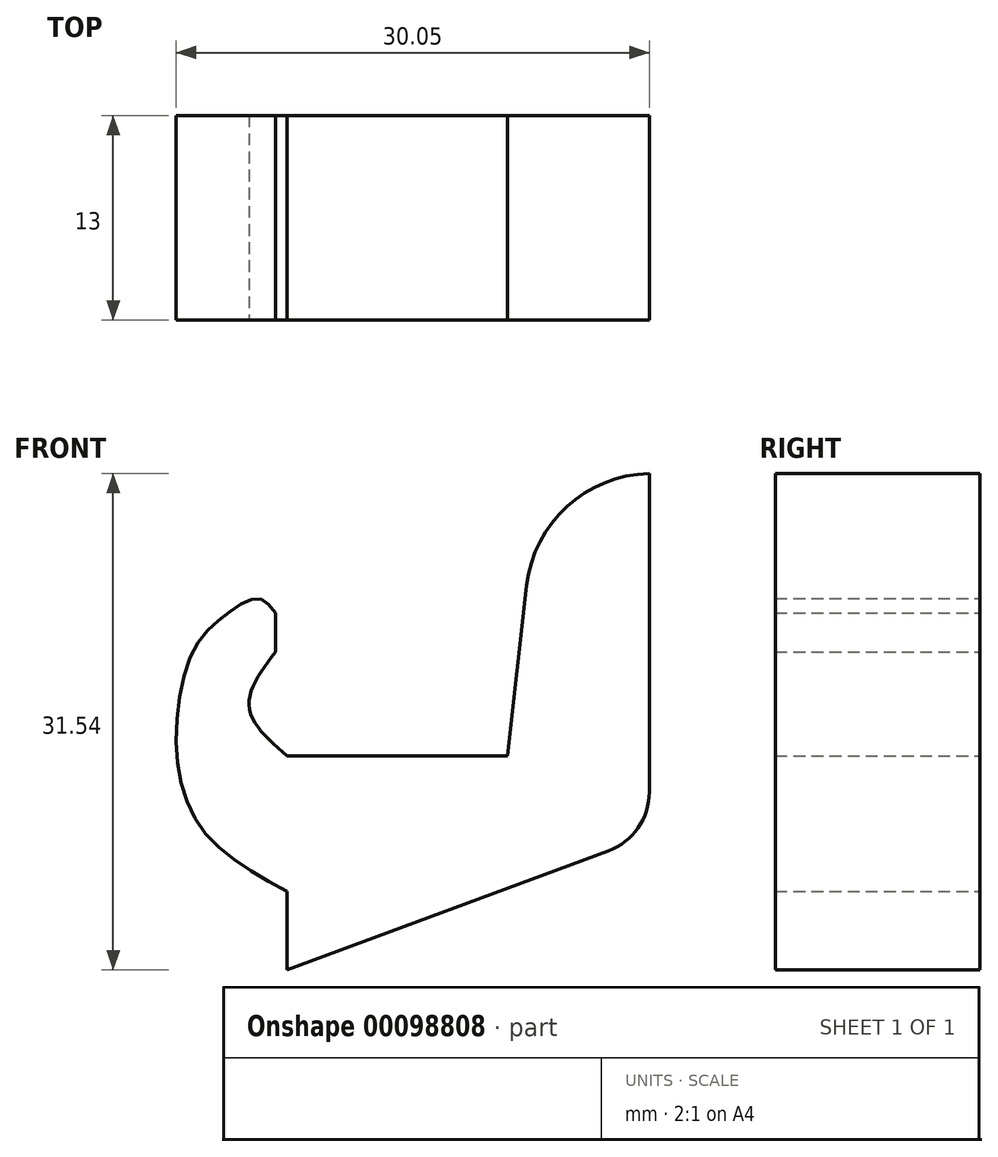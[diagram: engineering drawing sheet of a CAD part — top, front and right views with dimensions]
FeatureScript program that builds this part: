
annotation { "Feature Type Name" : "Feature", "Feature Type Description" : "" }
export const myFeature = defineFeature(function(context is Context, id is Id, definition is map)
    precondition{}
    {
        {
            var Q0;
            Q0=qCreatedBy(makeId("Front.planeOp"),FACE);
            var sketch = newSketch(context, id + "F0", { "sketchPlane" : qUnion([Q0])});
            skLineSegment(sketch, "E0", {"start": v(-14, 0) * mm, "end": v(0, 0) * mm});
            skLineSegment(sketch, "E1", {"start": v(0, 0) * mm, "end": v(0.37, 3.35) * mm});
            skLineSegment(sketch, "E2", {"start": v(2, 17.94) * mm, "end": v(9, 17.94) * mm});
            skLineSegment(sketch, "E3", {"start": v(9, 17.94) * mm, "end": v(9, -5.06) * mm});
            skLineSegment(sketch, "E4", {"start": v(9, -5.06) * mm, "end": v(-14, -13.6) * mm});
            skLineSegment(sketch, "E5", {"start": v(-14, -13.6) * mm, "end": v(-14, -8.6) * mm});
            skLineSegment(sketch, "E6", {"start": v(-14.75, 6.6) * mm, "end": v(-14.75, 9.1) * mm});
            skLineSegment(sketch, "E7", {"start": v(0.75, 6.7) * mm, "end": v(2, 17.94) * mm});
            skLineSegment(sketch, "E8", {"start": v(0.37, 3.35) * mm, "end": v(0.75, 6.7) * mm});
            skFitSpline(sketch, "E9", {"points": [v(-14.75, 9.1) * mm, v(-15.84, 10) * mm, v(-17.75, 9.08) * mm, v(-20, 6.6) * mm, v(-21, 0) * mm, v(-19, -5.14) * mm, v(-14, -8.6) * mm], "startDerivative": vector(-9.75, 12.65) * mm, "endDerivative": vector(27.06, -14.7) * mm});
            skFitSpline(sketch, "E10", {"points": [v(-14.75, 6.6) * mm, v(-16.43, 3.1) * mm, v(-14, 0) * mm], "startDerivative": vector(-5.4, -7.22) * mm, "endDerivative": vector(6.9, -5.98) * mm});
            skFitSpline(sketch, "E11", {"points": [v(-58.87, 22.86) * mm, v(-63.52, 20.49) * mm, v(-63.52, 20.01) * mm, v(-61.05, 15.08) * mm, v(-56.79, 18.12) * mm, v(-57.26, 25.7) * mm, v(-61.05, 22.76) * mm, v(-58.87, 22.86) * mm]});
            skSolve(sketch);
        }
        {
            var Q0;
            Q0=makeQuery(id+"F0.imprint","IMPRINT",FACE,{"disambiguationData":[TD([[makeQuery(id+"F0.imprint","IMPRINT",EDGE,{"derivedFrom":sQuery(id+"F0.wireOp",EDGE,"E0")}),-1.0]])]});
            extrude(context, id + "F1", {"entities" : qUnion([Q0]), "endBound" : BoundingType.SYMMETRIC, "depth" : 13 * mm});
        }
        {
            var Q0;
            Q0=makeQuery(id+"F1.opExtrude","SWEPT_EDGE",EDGE,{"disambiguationData":[OSD([sQuery(id+"F0.wireOp",EDGE,"E2"),sQuery(id+"F0.wireOp",EDGE,"E7")])]});
            fillet(context, id + "F2", {"entities" : qUnion([Q0]), "radius" : 8 * mm, "tangentPropagation" : true, "allowEdgeOverflow" : false});
        }
        {
            var Q0;
            Q0=makeQuery(id+"F1.opExtrude","SWEPT_EDGE",EDGE,{"disambiguationData":[OSD([sQuery(id+"F0.wireOp",EDGE,"E3"),sQuery(id+"F0.wireOp",EDGE,"E4")])]});
            fillet(context, id + "F3", {"entities" : qUnion([Q0]), "radius" : 4 * mm, "tangentPropagation" : true, "allowEdgeOverflow" : false});
        }
    });
